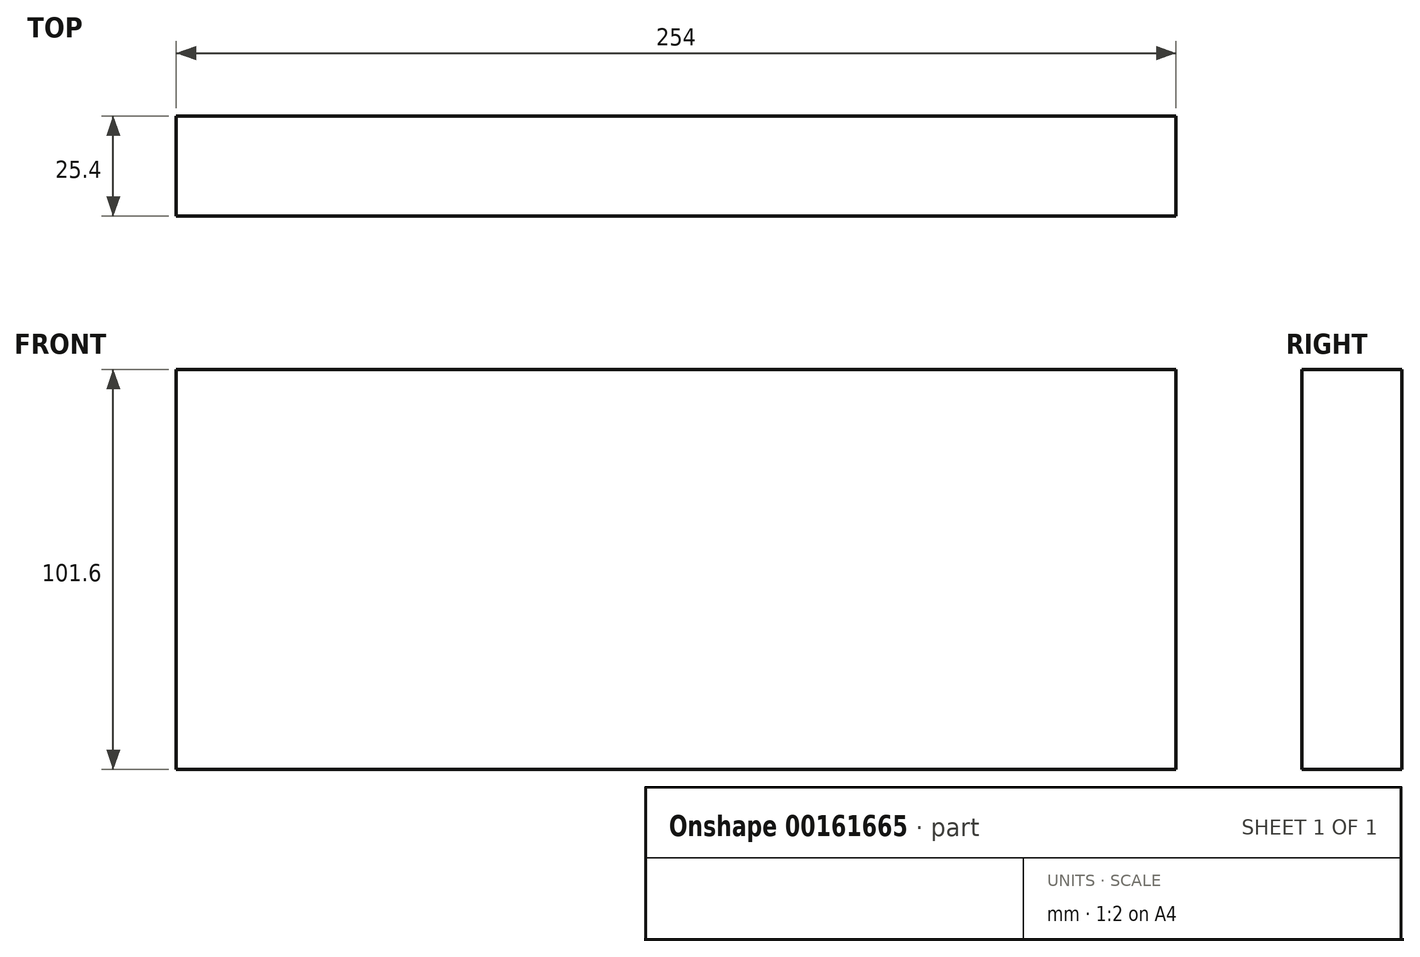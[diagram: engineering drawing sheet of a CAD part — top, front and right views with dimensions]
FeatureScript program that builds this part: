
annotation { "Feature Type Name" : "Feature", "Feature Type Description" : "" }
export const myFeature = defineFeature(function(context is Context, id is Id, definition is map)
    precondition{}
    {
        {
            var Q0;
            Q0=qCreatedBy(makeId("Front.planeOp"),FACE);
            var sketch = newSketch(context, id + "F0", { "sketchPlane" : qUnion([Q0])});
            skLineSegment(sketch, "E0.bottom", {"start": v(-127, 70.84) * mm, "end": v(127, 70.84) * mm});
            skLineSegment(sketch, "E0.top", {"start": v(-127, -30.76) * mm, "end": v(127, -30.76) * mm});
            skLineSegment(sketch, "E0.left", {"start": v(-127, 70.84) * mm, "end": v(-127, -30.76) * mm});
            skLineSegment(sketch, "E0.right", {"start": v(127, 70.84) * mm, "end": v(127, -30.76) * mm});
            skPoint(sketch, "E0.middle", {"position": v(0, 20.04) * mm});
            skSolve(sketch);
        }
        {
            var Q0;
            Q0=makeQuery(id+"F0.imprint","IMPRINT",FACE,{"disambiguationData":[TD([[makeQuery(id+"F0.imprint","IMPRINT",EDGE,{"derivedFrom":sQuery(id+"F0.wireOp",EDGE,"E0.bottom")}),-1.0]])]});
            extrude(context, id + "F1", {"entities" : qUnion([Q0]), "depth" : 25.4 * mm});
        }
    });
